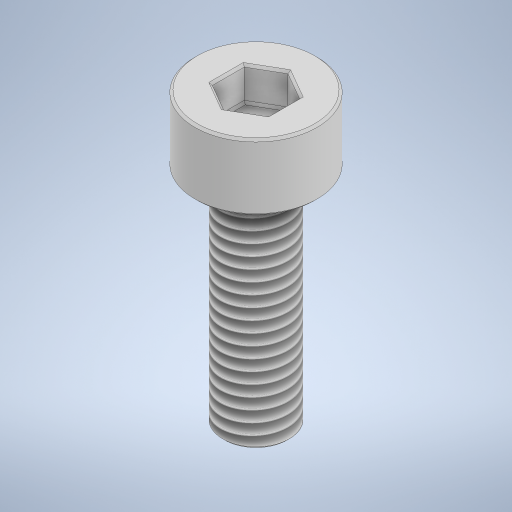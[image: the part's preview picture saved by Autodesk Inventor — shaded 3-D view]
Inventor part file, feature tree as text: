
AUTODESK INVENTOR PART (.ipt)
format: ipt  version: 2023 (Build 270158000, 158)  size: 315,392 bytes
history: native  units: in
note: dims shown in document units (in); Inventor stores cm internally (conversion verified against a paired STEP export)
features: sketch x2, revolve x1, thread x1, extrude x1, chamfer x1
ambient origin geometry x8: Origin, YZ Plane, XZ Plane, XY Plane, X Axis, Y Axis, Z Axis, Center Point
bodies: Solid1 (feature_tree)
feature tree (6):
  revolve  "Revolution1"  [1 undecoded]
  thread  "Thread1"  [1 undecoded]
  extrude  "Extrusion2"  TaperAngle=90.0deg  [1 undecoded]
  chamfer  "Chamfer2"  Distance=0.1181in
  sketch  "Sketch1"  dims[d0=0.1083in d1=0.1181in d2=0.3937in]
  sketch  "Sketch3"  dims[d3=0.0591in d4=90.0deg d5=0.1181in d6=0.0in d13=0.0984in d14=0.0591in d15=0.0in d16=0.0039in d17=0.0787in d18=45.0deg]
note: 3 required parameter values undecoded (feature->parameter linkage not recoverable at this tier; creation-order binding heuristic only, values carry confidence <= 0.55)